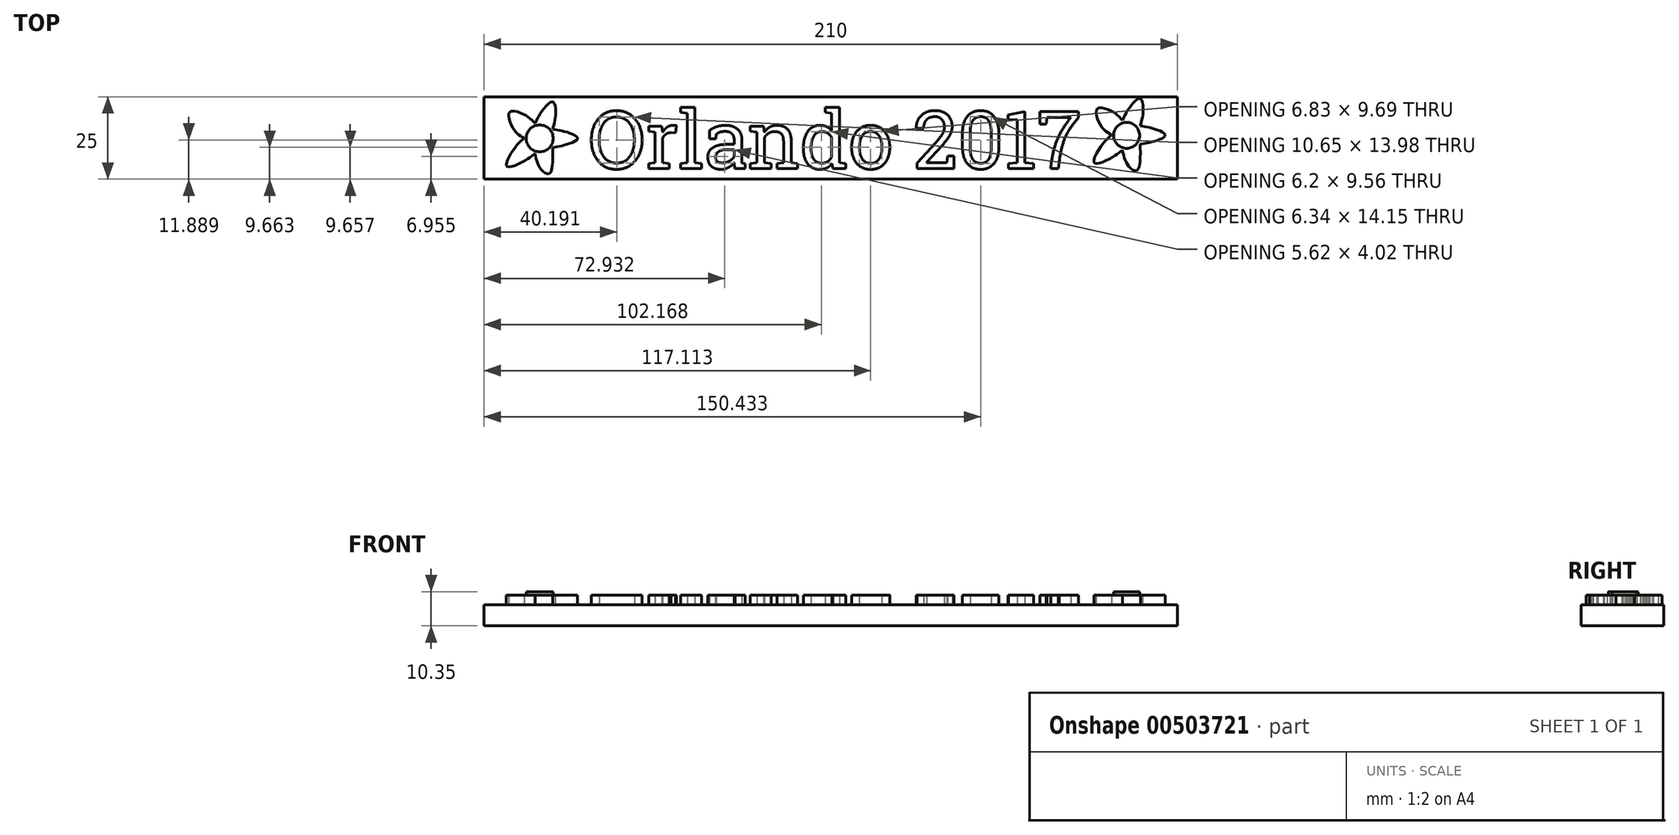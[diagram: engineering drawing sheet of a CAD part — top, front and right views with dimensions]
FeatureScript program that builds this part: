
annotation { "Feature Type Name" : "Feature", "Feature Type Description" : "" }
export const myFeature = defineFeature(function(context is Context, id is Id, definition is map)
    precondition{}
    {
        {
            var Q0;
            Q0=qCreatedBy(makeId("Top.planeOp"),FACE);
            var sketch = newSketch(context, id + "F0", { "sketchPlane" : qUnion([Q0])});
            skLineSegment(sketch, "E0.bottom", {"start": v(-57.56, 17.07) * mm, "end": v(152.44, 17.07) * mm});
            skLineSegment(sketch, "E0.top", {"start": v(-57.56, -7.93) * mm, "end": v(152.44, -7.93) * mm});
            skLineSegment(sketch, "E0.left", {"start": v(-57.56, 17.07) * mm, "end": v(-57.56, -7.93) * mm});
            skLineSegment(sketch, "E0.right", {"start": v(152.44, 17.07) * mm, "end": v(152.44, -7.93) * mm});
            skSolve(sketch);
        }
        {
            var Q0;
            Q0 = qSketchRegion(id + "F0", true);
            extrude(context, id + "F1", {"entities" : qUnion([Q0]), "depth" : 6.35 * mm, "offsetDistance" : 25 * mm});
        }
        {
            var Q0;
            Q0=makeQuery(id+"F1.opExtrude","CAP_FACE",FACE,{"disambiguationData":[OSD([sQuery(id+"F0.wireOp",EDGE,"E0.bottom"),sQuery(id+"F0.wireOp",EDGE,"E0.top"),sQuery(id+"F0.wireOp",EDGE,"E0.left"),sQuery(id+"F0.wireOp",EDGE,"E0.right")])],"isStart":false});
            var sketch = newSketch(context, id + "F2", { "sketchPlane" : qUnion([Q0])});
            skText(sketch, "E1", { "text": "Orlando 2017", "fontName": "RobotoSlab-Regular.ttf"});
            const initialGuessF2  = {"E1": [-0.02598, -0.0047, 1, 0, 0.01755]};
            skSetInitialGuess(sketch, initialGuessF2);
            skSolve(sketch);
        }
        {
            var Q0;
            Q0 = qSketchRegion(id + "F2", true);
            extrude(context, id + "F3", {"entities" : qUnion([Q0]), "depth" : 3 * mm, "offsetDistance" : 25 * mm});
        }
        {
            var Q0;
            {var subQ0=sQuery(id+"F0.wireOp",EDGE,"E0.left");var subQ1=sQuery(id+"F0.wireOp",EDGE,"E0.top");var subQ2=sQuery(id+"F0.wireOp",EDGE,"E0.right");var subQ3=sQuery(id+"F0.wireOp",EDGE,"E0.bottom");Q0=makeQuery(id+"F3.boolean.opBoolean","SPLIT",FACE,{"disambiguationData":[TD([makeQuery(id+"F1.opExtrude","SWEPT_FACE",FACE,{"disambiguationData":[OSD([subQ3])]})])],"derivedFrom":makeQuery(id+"F1.opExtrude","CAP_FACE",FACE,{"disambiguationData":[OSD([subQ3,subQ1,subQ0,subQ2])],"isStart":false})});}
            var sketch = newSketch(context, id + "F4", { "sketchPlane" : qUnion([Q0])});
            skCircle(sketch, "E2.cCircle", {"center": v(-40.64, 4.44) * mm, "radius": 3.85 * mm, "construction": true});
            skLineSegment(sketch, "E2.0", {"start": v(-36.79, 7.24) * mm, "end": v(-36.79, 1.64) * mm});
            skLineSegment(sketch, "E2.1", {"start": v(-36.79, 1.64) * mm, "end": v(-42.1, -0.08) * mm});
            skLineSegment(sketch, "E2.2", {"start": v(-42.1, -0.08) * mm, "end": v(-45.4, 4.44) * mm});
            skLineSegment(sketch, "E2.3", {"start": v(-45.4, 4.44) * mm, "end": v(-42.1, 8.97) * mm});
            skLineSegment(sketch, "E2.4", {"start": v(-42.1, 8.97) * mm, "end": v(-36.79, 7.24) * mm});
            skPoint(sketch, "E2.0.midPoint", {"position": v(-36.79, 4.44) * mm});
            skFitSpline(sketch, "E3", {"points": [v(-42.1, 8.97) * mm, v(-40.43, 12.12) * mm, v(-36.79, 15.54) * mm, v(-35.91, 11.27) * mm, v(-36.79, 7.24) * mm], "startDerivative": vector(5.24, 12.04) * mm, "endDerivative": vector(-4.6, -14.24) * mm});
            skFitSpline(sketch, "E4", {"points": [v(-36.79, 7.24) * mm, v(-32.25, 6.27) * mm, v(-29.2, 4.44) * mm, v(-32.5, 2.6) * mm, v(-36.79, 1.64) * mm], "startDerivative": vector(16.18, -2.5) * mm, "endDerivative": vector(-15.37, -2.72) * mm});
            skFitSpline(sketch, "E5", {"points": [v(-36.79, 1.64) * mm, v(-36.79, -2.88) * mm, v(-37.87, -6.3) * mm, v(-40.55, -4.59) * mm, v(-42.1, -0.08) * mm], "startDerivative": vector(0.6, -16.17) * mm, "endDerivative": vector(-3.36, 17.44) * mm});
            skFitSpline(sketch, "E6", {"points": [v(-42.1, 8.97) * mm, v(-45.3, 11.64) * mm, v(-49.82, 12.37) * mm, v(-48.6, 7.24) * mm, v(-45.4, 4.44) * mm], "startDerivative": vector(-10.8, 11.7) * mm, "endDerivative": vector(13.84, -8.26) * mm});
            skFitSpline(sketch, "E7", {"points": [v(-45.4, 4.44) * mm, v(-48.23, 1.64) * mm, v(-50.67, -3.98) * mm, v(-45.4, -2.4) * mm, v(-42.1, -0.08) * mm], "startDerivative": vector(-11.5, -8.85) * mm, "endDerivative": vector(11.36, 9.38) * mm});
            skCircle(sketch, "E8.cCircle", {"center": v(137.34, 5.42) * mm, "radius": 3.85 * mm, "construction": true});
            skLineSegment(sketch, "E8.0", {"start": v(141.18, 8.22) * mm, "end": v(141.18, 2.62) * mm});
            skLineSegment(sketch, "E8.1", {"start": v(141.18, 2.62) * mm, "end": v(135.87, 0.9) * mm});
            skFitSpline(sketch, "E9", {"points": [v(135.87, 9.95) * mm, v(137.54, 13.1) * mm, v(141.18, 16.52) * mm, v(142.06, 12.25) * mm, v(141.18, 8.22) * mm], "startDerivative": vector(5.24, 12.04) * mm, "endDerivative": vector(-4.6, -14.24) * mm});
            skFitSpline(sketch, "E10", {"points": [v(141.18, 8.22) * mm, v(145.72, 7.25) * mm, v(148.77, 5.42) * mm, v(145.47, 3.59) * mm, v(141.18, 2.62) * mm], "startDerivative": vector(16.18, -2.5) * mm, "endDerivative": vector(-15.37, -2.72) * mm});
            skFitSpline(sketch, "E11", {"points": [v(141.18, 2.62) * mm, v(141.18, -1.9) * mm, v(140.1, -5.32) * mm, v(137.42, -3.6) * mm, v(135.87, 0.9) * mm], "startDerivative": vector(0.6, -16.17) * mm, "endDerivative": vector(-3.36, 17.44) * mm});
            skFitSpline(sketch, "E12", {"points": [v(135.87, 9.95) * mm, v(132.66, 12.62) * mm, v(128.15, 13.35) * mm, v(129.37, 8.22) * mm, v(132.58, 5.42) * mm], "startDerivative": vector(-10.8, 11.7) * mm, "endDerivative": vector(13.84, -8.26) * mm});
            skFitSpline(sketch, "E13", {"points": [v(132.58, 5.42) * mm, v(129.74, 2.62) * mm, v(127.3, -3) * mm, v(132.58, -1.41) * mm, v(135.87, 0.9) * mm], "startDerivative": vector(-11.5, -8.85) * mm, "endDerivative": vector(11.36, 9.38) * mm});
            skSolve(sketch);
        }
        {
            var Q0;
            Q0=makeQuery(id+"F4.imprint","IMPRINT",FACE,{"disambiguationData":[TD([[makeQuery(id+"F4.imprint","IMPRINT",EDGE,{"derivedFrom":sQuery(id+"F4.wireOp",EDGE,"E2.0")}),-1.0]])]});
            var Q1;
            Q1=makeQuery(id+"F4.imprint","IMPRINT",FACE,{"disambiguationData":[TD([[makeQuery(id+"F4.imprint","IMPRINT",EDGE,{"derivedFrom":sQuery(id+"F4.wireOp",EDGE,"E2.4")}),1.0]])]});
            var Q2;
            Q2=makeQuery(id+"F4.imprint","IMPRINT",FACE,{"disambiguationData":[TD([[makeQuery(id+"F4.imprint","IMPRINT",EDGE,{"derivedFrom":sQuery(id+"F4.wireOp",EDGE,"E2.0")}),1.0]])]});
            var Q3;
            Q3=makeQuery(id+"F4.imprint","IMPRINT",FACE,{"disambiguationData":[TD([[makeQuery(id+"F4.imprint","IMPRINT",EDGE,{"derivedFrom":sQuery(id+"F4.wireOp",EDGE,"E2.1")}),1.0]])]});
            var Q4;
            Q4=makeQuery(id+"F4.imprint","IMPRINT",FACE,{"disambiguationData":[TD([[makeQuery(id+"F4.imprint","IMPRINT",EDGE,{"derivedFrom":sQuery(id+"F4.wireOp",EDGE,"E2.2")}),1.0]])]});
            var Q5;
            Q5=makeQuery(id+"F4.imprint","IMPRINT",FACE,{"disambiguationData":[TD([[makeQuery(id+"F4.imprint","IMPRINT",EDGE,{"derivedFrom":sQuery(id+"F4.wireOp",EDGE,"E2.3")}),1.0]])]});
            var Q6;
            Q6=makeQuery(id+"F4.imprint","IMPRINT",FACE,{"disambiguationData":[TD([[makeQuery(id+"F4.imprint","IMPRINT",EDGE,{"derivedFrom":sQuery(id+"F4.wireOp",EDGE,"E8.0")}),-1.0]])]});
            var Q7;
            Q7=makeQuery(id+"F4.imprint","IMPRINT",FACE,{"disambiguationData":[TD([[makeQuery(id+"F4.imprint","IMPRINT",EDGE,{"derivedFrom":sQuery(id+"F4.wireOp",EDGE,"E8.0")}),1.0]])]});
            var Q8;
            Q8=makeQuery(id+"F4.imprint","IMPRINT",FACE,{"disambiguationData":[TD([[makeQuery(id+"F4.imprint","IMPRINT",EDGE,{"derivedFrom":sQuery(id+"F4.wireOp",EDGE,"E8.1")}),1.0]])]});
            extrude(context, id + "F5", {"entities" : qUnion([Q0, Q1, Q2, Q3, Q4, Q5, Q6, Q7, Q8]), "operationType" : NewBodyOperationType.ADD, "depth" : 3 * mm, "offsetDistance" : 25 * mm});
        }
        {
            var Q0;
            Q0=makeQuery(id+"F5.opExtrude","CAP_FACE",FACE,{"disambiguationData":[OSD([sQuery(id+"F4.wireOp",EDGE,"E3"),sQuery(id+"F4.wireOp",EDGE,"E4"),sQuery(id+"F4.wireOp",EDGE,"E5"),sQuery(id+"F4.wireOp",EDGE,"E6"),sQuery(id+"F4.wireOp",EDGE,"E7")])],"isStart":false});
            var sketch = newSketch(context, id + "F6", { "sketchPlane" : qUnion([Q0])});
            skCircle(sketch, "E14", {"center": v(-40.7, 4.45) * mm, "radius": 4.08 * mm});
            skCircle(sketch, "E15", {"center": v(137.08, 5.36) * mm, "radius": 3.93 * mm});
            skSolve(sketch);
        }
        {
            var Q0;
            Q0=makeQuery(id+"F6.imprint","IMPRINT",FACE,{"disambiguationData":[TD([[makeQuery(id+"F6.imprint","IMPRINT",EDGE,{"derivedFrom":sQuery(id+"F6.wireOp",EDGE,"E14")}),1.0]])]});
            var Q1;
            Q1=makeQuery(id+"F6.imprint","IMPRINT",FACE,{"disambiguationData":[TD([[makeQuery(id+"F6.imprint","IMPRINT",EDGE,{"derivedFrom":sQuery(id+"F6.wireOp",EDGE,"E15")}),1.0]])]});
            var Q2;
            Q2=sQuery(id+"F6.wireOp",EDGE,"E14");
            var Q3;
            Q3=sQuery(id+"F6.wireOp",EDGE,"E15");
            extrude(context, id + "F7", {"entities" : qUnion([Q0, Q1]), "operationType" : NewBodyOperationType.ADD, "surfaceEntities" : qUnion([Q2, Q3]), "depth" : 1 * mm, "offsetDistance" : 25 * mm});
        }
    });
